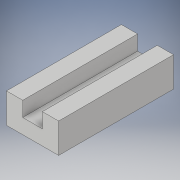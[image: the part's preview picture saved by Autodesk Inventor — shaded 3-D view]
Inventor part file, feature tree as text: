
AUTODESK INVENTOR PART (.ipt)
format: ipt  version: 2017 (Build 210142000, 142)  size: 119,296 bytes
history: native  units: in
note: dims shown in document units (in); Inventor stores cm internally (conversion verified against a paired STEP export)
features: sketch x2, extrude x1, hole x1
ambient origin geometry x8: Origin, YZ Plane, XZ Plane, XY Plane, X Axis, Y Axis, Z Axis, Center Point
bodies: Solid1 (feature_tree)
feature tree (4):
  extrude  "Extrusion1"  Depth=1.0in
  hole  "Hole1"  [1 undecoded]
  sketch  "Sketch1"  dims[d0=1.75in d1=1.0in]
  sketch  "Sketch2"  dims[d2=0.66in d4=0.545in d5=0.545in d6=0.5in d7=3.855in d8=0.0in d9=0.2275in d10=0.2275in d11=0.875in d12=0.875in d13=0.2275in d14=0.2275in d15=0.875in d16=0.875in d17=2.105in d18=2.105in d19=0.15in d20=0.75in d21=0.375in d22=0.25in d23=0.5635in d24=0.3in d25=0.0in]
note: 1 required parameter value undecoded (feature->parameter linkage not recoverable at this tier; creation-order binding heuristic only, values carry confidence <= 0.55)
